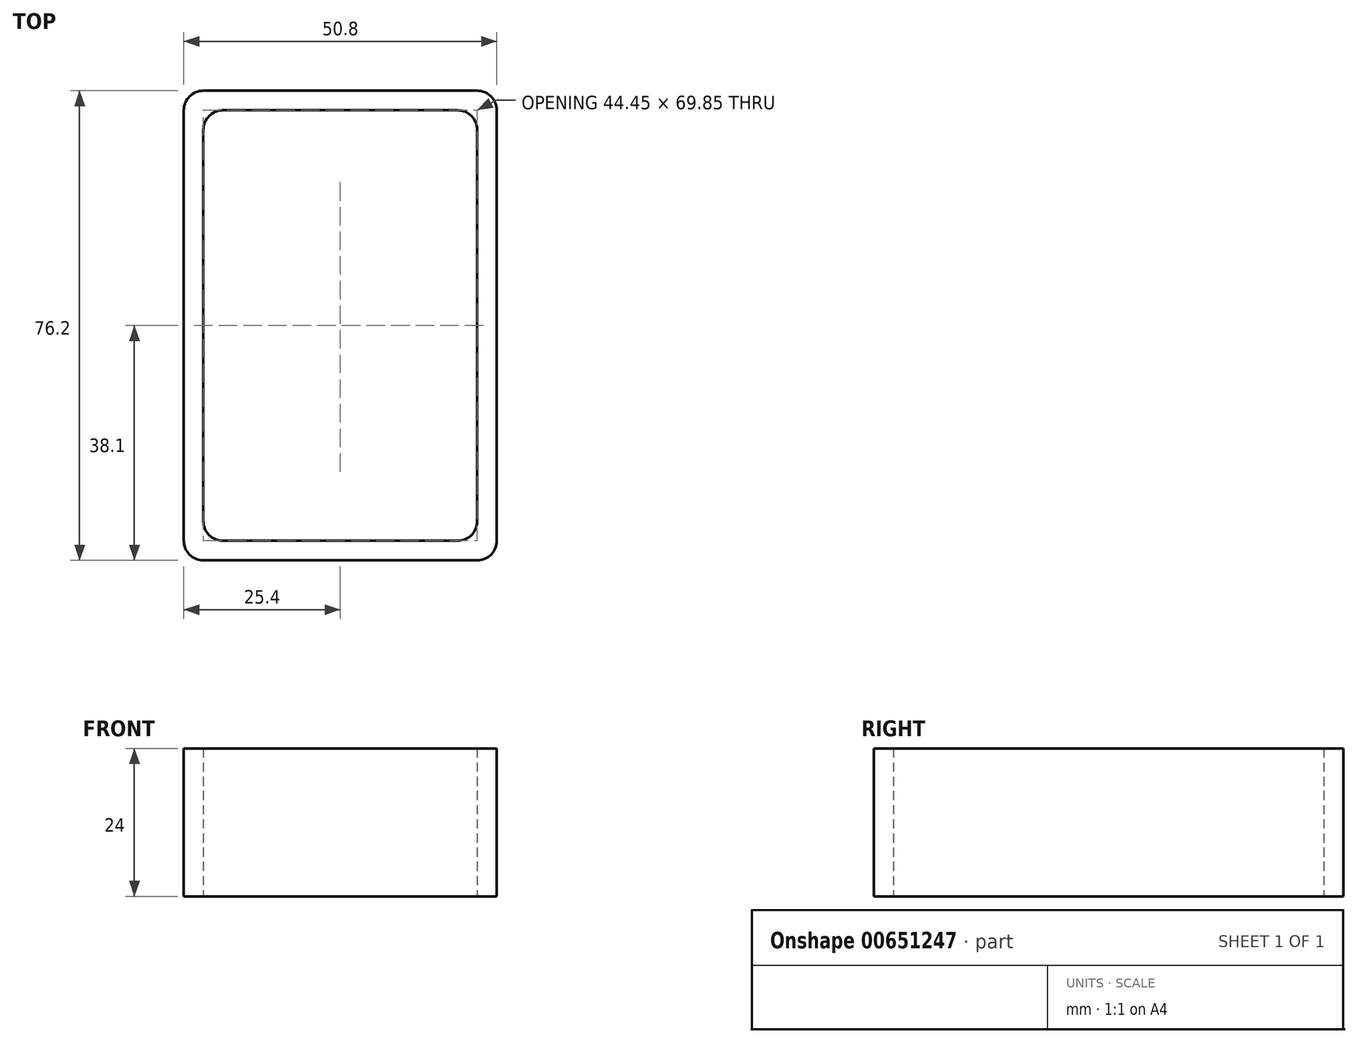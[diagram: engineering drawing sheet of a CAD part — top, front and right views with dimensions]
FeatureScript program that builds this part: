
annotation { "Feature Type Name" : "Feature", "Feature Type Description" : "" }
export const myFeature = defineFeature(function(context is Context, id is Id, definition is map)
    precondition{}
    {
        {
            var Q0;
            Q0=qCreatedBy(makeId("Top.planeOp"),FACE);
            var sketch = newSketch(context, id + "F0", { "sketchPlane" : qUnion([Q0])});
            skLineSegment(sketch, "E0.bottom", {"start": v(-25.4, 38.1) * mm, "end": v(25.4, 38.1) * mm});
            skLineSegment(sketch, "E0.top", {"start": v(-25.4, -38.1) * mm, "end": v(25.4, -38.1) * mm});
            skLineSegment(sketch, "E0.left", {"start": v(-25.4, 38.1) * mm, "end": v(-25.4, -38.1) * mm});
            skLineSegment(sketch, "E0.right", {"start": v(25.4, 38.1) * mm, "end": v(25.4, -38.1) * mm});
            skPoint(sketch, "E0.middle", {"position": v(0, 0) * mm});
            skLineSegment(sketch, "E1.bottom", {"start": v(-22.23, 34.93) * mm, "end": v(22.22, 34.93) * mm});
            skLineSegment(sketch, "E1.top", {"start": v(-22.23, -34.93) * mm, "end": v(22.22, -34.93) * mm});
            skLineSegment(sketch, "E1.left", {"start": v(-22.23, 34.93) * mm, "end": v(-22.23, -34.93) * mm});
            skLineSegment(sketch, "E1.right", {"start": v(22.22, 34.93) * mm, "end": v(22.22, -34.93) * mm});
            skSolve(sketch);
        }
        {
            assignVariable(context, id + "F1", {"name" : "Length", "anyValue" : 24});
        }
        {
            var Q0;
            Q0=makeQuery(id+"F0.imprint","IMPRINT",FACE,{"disambiguationData":[TD([[makeQuery(id+"F0.imprint","IMPRINT",EDGE,{"derivedFrom":sQuery(id+"F0.wireOp",EDGE,"E0.bottom")}),-1.0]])]});
            extrude(context, id + "F2", {"entities" : qUnion([Q0]), "depth" : (getVariable(context, 'Length')) * mm, "offsetDistance" : 25.4 * mm});
        }
        {
            var Q0;
            Q0=makeQuery(id+"F2.opExtrude","SWEPT_EDGE",EDGE,{"disambiguationData":[OSD([sQuery(id+"F0.wireOp",EDGE,"E1.bottom"),sQuery(id+"F0.wireOp",EDGE,"E1.left")])]});
            var Q1;
            Q1=makeQuery(id+"F2.opExtrude","SWEPT_EDGE",EDGE,{"disambiguationData":[OSD([sQuery(id+"F0.wireOp",EDGE,"E1.bottom"),sQuery(id+"F0.wireOp",EDGE,"E1.right")])]});
            var Q2;
            Q2=makeQuery(id+"F2.opExtrude","SWEPT_EDGE",EDGE,{"disambiguationData":[OSD([sQuery(id+"F0.wireOp",EDGE,"E1.top"),sQuery(id+"F0.wireOp",EDGE,"E1.right")])]});
            var Q3;
            Q3=makeQuery(id+"F2.opExtrude","SWEPT_EDGE",EDGE,{"disambiguationData":[OSD([sQuery(id+"F0.wireOp",EDGE,"E1.top"),sQuery(id+"F0.wireOp",EDGE,"E1.left")])]});
            var Q4;
            Q4=makeQuery(id+"F2.opExtrude","SWEPT_EDGE",EDGE,{"disambiguationData":[OSD([sQuery(id+"F0.wireOp",EDGE,"E0.bottom"),sQuery(id+"F0.wireOp",EDGE,"E0.right")])]});
            var Q5;
            Q5=makeQuery(id+"F2.opExtrude","SWEPT_EDGE",EDGE,{"disambiguationData":[OSD([sQuery(id+"F0.wireOp",EDGE,"E0.bottom"),sQuery(id+"F0.wireOp",EDGE,"E0.left")])]});
            var Q6;
            Q6=makeQuery(id+"F2.opExtrude","SWEPT_EDGE",EDGE,{"disambiguationData":[OSD([sQuery(id+"F0.wireOp",EDGE,"E0.top"),sQuery(id+"F0.wireOp",EDGE,"E0.right")])]});
            var Q7;
            Q7=makeQuery(id+"F2.opExtrude","SWEPT_EDGE",EDGE,{"disambiguationData":[OSD([sQuery(id+"F0.wireOp",EDGE,"E0.top"),sQuery(id+"F0.wireOp",EDGE,"E0.left")])]});
            fillet(context, id + "F3", {"entities" : qUnion([Q0, Q1, Q2, Q3, Q4, Q5, Q6, Q7]), "radius" : 3.17 * mm, "tangentPropagation" : true, "allowEdgeOverflow" : false});
        }
    });
